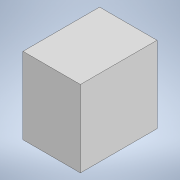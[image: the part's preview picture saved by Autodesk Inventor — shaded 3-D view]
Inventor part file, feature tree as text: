
AUTODESK INVENTOR PART (.ipt)
format: ipt  version: 2021 (Build 250183000, 183)  size: 93,696 bytes
history: native  units: mm
features: other x1, extrude x1, sketch x1
ambient origin geometry x8: Origin, YZ Plane, XZ Plane, XY Plane, X Axis, Y Axis, Z Axis, Center Point
bodies: Body1 (feature_tree)
feature tree (3):
  other  "ソリッド1"
  extrude  "押し出し1"  Depth=2000.0mm TaperAngle=0.0deg
  sketch  "スケッチ1"
